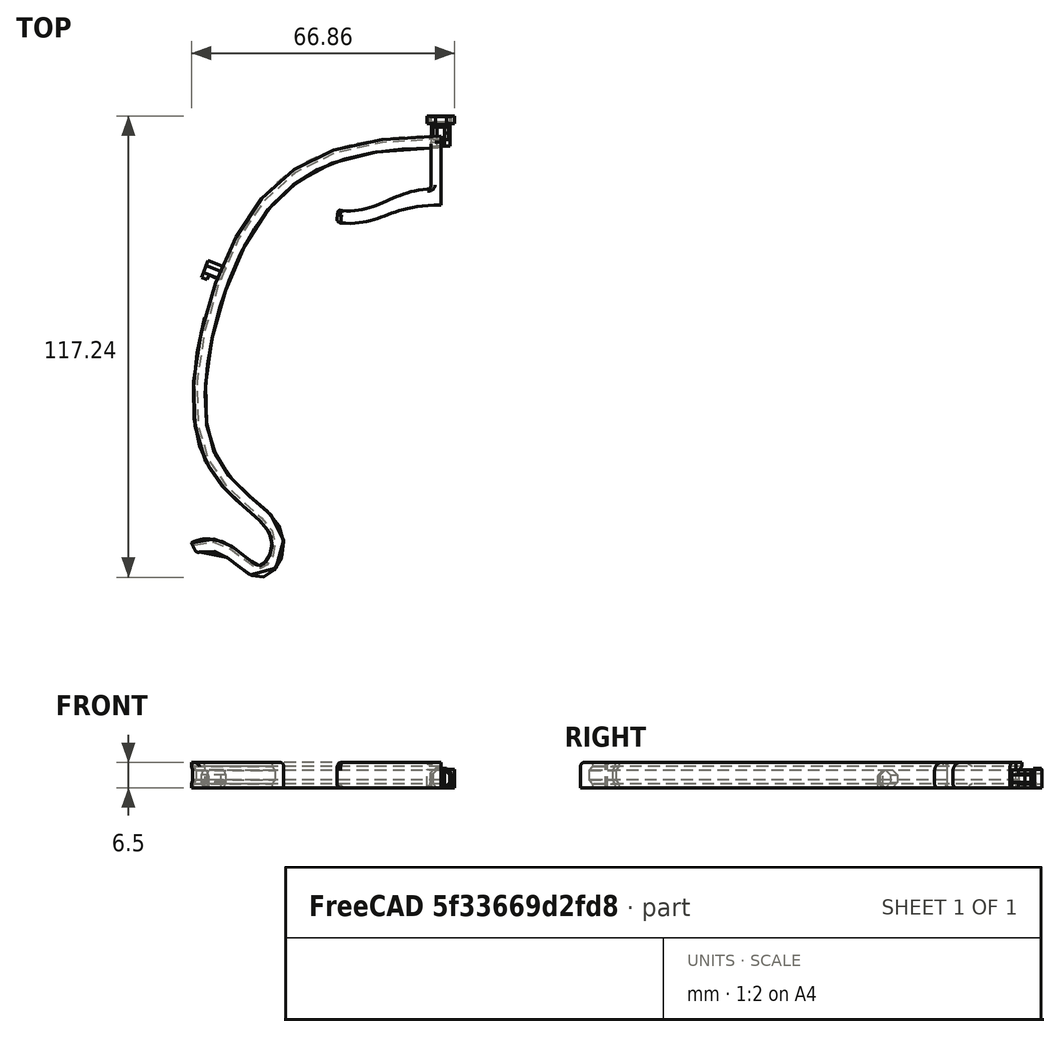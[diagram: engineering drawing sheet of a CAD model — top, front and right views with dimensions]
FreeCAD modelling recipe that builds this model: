
FCSTD DOCUMENT  (FreeCAD 0.18R16146 (Git))
Label: frame-001-02-c
License: All rights reserved
LicenseURL: http://ja.wikipedia.org/wiki/%E8%91%97%E4%BD%9C%E6%A8%A9%E8%A1%A8%E7%A4%BA
objects: Sketcher::SketchObject×5, Part::Extrusion×5, Part::Box×3, Part::Cut×2, Part::Fillet×2, Part::Compound×2, Mesh::Feature×1, Part::Sweep×1, Part::Mirroring×1, Part::MultiCommon×1
note: 22 computed .brp shape members not serialized (recipe doc carries the construction recipe); baked Part::Feature solids carry a one-line shape summary decoded from their .brp

FEATURE [Sketcher::SketchObject] Sketch  label="Sketch_FrameShape"
  sketch-geometry (15):
    g0-g7: Circle [constr] x8 (B-spline internal-alignment scaffolding for g8; pole/knot coordinates omitted)
    g8: BSplineCurve PolesCount=8 KnotsCount=6 Degree=3 IsPeriodic=0
    g9-g14: GeomPoint [constr] x6 (B-spline internal-alignment scaffolding for g8; pole/knot coordinates omitted)
  constraints (6):
    c: Radius(g0) = 6
    c: Equal(g0, g1-g6) x6
    c: InternalAlignment(g0-g7 -> g8) x8
    c: InternalAlignment(g9-g14 -> g8) x6
    c: Horizontal(g1,g8)
    c: Coincident(g-1,g8)
FEATURE [Sketcher::SketchObject] Sketch001
  Placement = pos=(0,0,0) rot=(0.57735,0.57735,0.57735;2.0944rad)
  sketch-geometry (8):
    g0: LineSegment StartX=-0.5 StartY=6.5 StartZ=0 EndX=2.5 EndY=6.5 EndZ=0
    g1: LineSegment StartX=2.5 StartY=6.5 StartZ=0 EndX=2.5 EndY=5.5 EndZ=0
    g2: LineSegment StartX=2.5 StartY=0 StartZ=0 EndX=-0.5 EndY=0 EndZ=0
    g3: LineSegment StartX=-0.5 StartY=0 StartZ=0 EndX=-0.5 EndY=6.5 EndZ=0
    g4: LineSegment StartX=2.5 StartY=5.5 StartZ=0 EndX=1.7 EndY=4.5 EndZ=0
    g5: LineSegment StartX=1.7 StartY=4.5 StartZ=0 EndX=1.7 EndY=2 EndZ=0
    g6: LineSegment StartX=1.7 StartY=2 StartZ=0 EndX=2.5 EndY=1 EndZ=0
    g7: LineSegment StartX=2.5 StartY=1 StartZ=0 EndX=2.5 EndY=0 EndZ=0
  constraints (24):
    c: Coincident(g0,g1)
    c: Coincident(g2,g3)
    c: Coincident(g3,g0)
    c: Horizontal(g0)
    c: Horizontal(g2)
    c: Vertical(g1)
    c: Vertical(g3)
    c: DistanceX(g0,g0) = 3
    c: DistanceY(g1,g0) = 1
    c: DistanceX(g-1,g2) = -0.5
    c: PointOnObject(g2,g-1)
    c: DistanceY(g2,g0) = 6.5
    c: Coincident(g1,g4)
    c: Coincident(g4,g5)
    c: Vertical(g5)
    c: Coincident(g5,g6)
    c: Coincident(g6,g7)
    c: Coincident(g7,g2)
    c: DistanceX(g2,g2) = 3
    c: Vertical(g7)
    c: DistanceY(g2,g6) = 1
    c: DistanceY(g6,g5) = 1
    c: DistanceY(g4,g1) = 1
    c: DistanceX(g2,g5) = 2.2
FEATURE [Mesh::Feature] cd43cbcc_75a4_11ea_893f_42010a00001e_UM3E_Visor_frame_EUROPE_ISO838_v3  label="cd43cbcc-75a4-11ea-893f-42010a00001e_UM3E_Visor_frame_EUROPE_ISO838_v3"
  Placement = pos=(0,-59,0) rot=(0,0,1;0rad)
FEATURE [Sketcher::SketchObject] Sketch002  label="OctPinSketch"
  Placement = pos=(0,0,0) rot=(1,0,0;1.5708rad)
  sketch-geometry (9):
    g0: LineSegment StartX=2.3097 StartY=1.35299 StartZ=0 EndX=2.3097 EndY=3.26641 EndZ=0
    g1: LineSegment StartX=2.3097 StartY=3.26641 StartZ=0 EndX=0.956709 EndY=4.6194 EndZ=0
    g2: LineSegment StartX=0.956709 StartY=4.6194 StartZ=0 EndX=-0.956709 EndY=4.6194 EndZ=0
    g3: LineSegment StartX=-0.956709 StartY=4.6194 StartZ=0 EndX=-2.3097 EndY=3.26641 EndZ=0
    g4: LineSegment StartX=-2.3097 StartY=3.26641 StartZ=0 EndX=-2.3097 EndY=1.35299 EndZ=0
    g5: LineSegment StartX=-2.3097 StartY=1.35299 StartZ=0 EndX=-0.956709 EndY=0 EndZ=0
    g6: LineSegment StartX=-0.956709 StartY=0 StartZ=0 EndX=0.956709 EndY=0 EndZ=0
    g7: LineSegment StartX=0.956709 StartY=0 StartZ=0 EndX=2.3097 EndY=1.35299 EndZ=0
    g8: Circle [constr] CenterX=0 CenterY=2.3097 CenterZ=0 NormalX=0 NormalY=0 NormalZ=1 AngleXU=0 Radius=2.5
  constraints (21):
    c: Coincident(g0,g1)
    c: Coincident(g1,g2)
    c: Coincident(g2,g3)
    c: Coincident(g3,g4)
    c: Coincident(g4,g5)
    c: Coincident(g5,g6)
    c: Coincident(g6,g7)
    c: Coincident(g7,g0)
    c: Equal(g0, g1-g7) x7
    c: PointOnObject(g0,g8)
    c: PointOnObject(g1,g8)
    c: PointOnObject(g2,g8)
    c: PointOnObject(g3,g8)
    c: PointOnObject(g4,g8)
    c: PointOnObject(g5,g8)
    c: PointOnObject(g6,g8)
    c: PointOnObject(g7,g8)
    c: Distance(g0,g8) = 2.5
    c: Horizontal(g6)
    c: PointOnObject(g8,g-2)
    c: PointOnObject(g6,g-1)
FEATURE [Part::Extrusion] Extrude002  label="OctPin"
  Base = -> Sketch002
  Dir = (0,-1,0)
  DirMode = 2
  FaceMakerClass = Part::FaceMakerBullseye
  LengthFwd = -6
  LengthRev = 0
  Solid = true
  Symmetric = false
FEATURE [Part::Extrusion] Extrude003  label="OctPinFront"
  Base = -> Sketch002
  Dir = (0,-1,2e-16)
  DirMode = 2
  FaceMakerClass = Part::FaceMakerBullseye
  LengthFwd = -3.8
  LengthRev = 0
  Placement = pos=(0,3,0) rot=(0,0,1;0rad)
  Solid = true
  Symmetric = false
FEATURE [Part::Extrusion] Extrude004  label="OctPin_WNotch_column"
  Base = -> Sketch002
  Dir = (0,-1,2e-16)
  DirMode = 2
  FaceMakerClass = Part::FaceMakerBullseye
  LengthFwd = -4.8
  LengthRev = 0
  Solid = true
  Symmetric = false
FEATURE [Part::Box] Box008  label="立方体008"
  AttacherType = Attacher::AttachEngine3D
  Height = 6
  Length = 2
  Placement = pos=(1,0,-0.5) rot=(0,0,1;0rad)
  Width = 3.3
FEATURE [Part::Cut] Cut  label="OctPin_WNotch"
  Base = -> Extrude004
  Tool = -> Box008
FEATURE [Part::Cut] Cut001  label="OctPin_WNotchR"
  Base = -> Extrude004
  Placement = pos=(55.5,-33.1,0) rot=(0,0,-1;1.18682rad)
  Tool = -> Box008
FEATURE [Sketcher::SketchObject] Sketch003
  sketch-geometry (18):
    g0: LineSegment StartX=0 StartY=1 StartZ=0 EndX=0 EndY=-15 EndZ=0
    g1: LineSegment StartX=2.5 StartY=-11 StartZ=0 EndX=2.5 EndY=1 EndZ=0
    g2: LineSegment StartX=2.5 StartY=1 StartZ=0 EndX=0 EndY=1 EndZ=0
    g3: LineSegment StartX=26.0693 StartY=-16.3 StartZ=0 EndX=26.4803 EndY=-19.4735 EndZ=0
    g4-g7: Circle [constr] x4 (B-spline internal-alignment scaffolding for g8; pole/knot coordinates omitted)
    g8: BSplineCurve PolesCount=4 KnotsCount=2 Degree=3 IsPeriodic=0
    g9: GeomPoint [constr] X=2.5 Y=-11 Z=0
    g10: GeomPoint [constr] X=26.0693 Y=-16.3 Z=0
    g11-g14: Circle [constr] x4 (B-spline internal-alignment scaffolding for g15; pole/knot coordinates omitted)
    g15: BSplineCurve PolesCount=4 KnotsCount=2 Degree=3 IsPeriodic=0
    g16: GeomPoint [constr] X=0 Y=-15 Z=0
    g17: GeomPoint [constr] X=26.4803 Y=-19.4735 Z=0
  constraints (32):
    c: PointOnObject(g0,g-2)
    c: Vertical(g0)
    c: Vertical(g1)
    c: Coincident(g1,g2)
    c: Coincident(g2,g0)
    c: DistanceX(g0,g1) = 2.5
    c: Horizontal(g2)
    c: DistanceY(g-1,g0) = 1
    c: DistanceY(g3,g1) = 5.3
    c: DistanceY(g0,g1) = 4
    c: DistanceY(g0,g-1) = 15
    c: Coincident(g8,g1)
    c: Radius(g4) = 2
    c: Equal(g4,g5)
    c: Equal(g4,g6)
    c: Equal(g4,g7)
    c: Coincident(g8,g3)
    c: InternalAlignment(g4-g7 -> g8) x4
    c: InternalAlignment(g9,g8)
    c: InternalAlignment(g10,g8)
    c: Coincident(g15,g0)
    c: Radius(g11) = 2
    c: Equal(g11,g12)
    c: Equal(g11,g13)
    c: Equal(g11,g14)
    c: Coincident(g15,g3)
    c: InternalAlignment(g11-g14 -> g15) x4
    c: InternalAlignment(g16,g15)
    c: InternalAlignment(g17,g15)
    c: Distance(g3,g3) = 3.2
    c: Horizontal(g0,g12)
    c: Horizontal(g5,g1)
FEATURE [Part::Extrusion] Extrude
  Base = -> Sketch003
  Dir = (0,0,1)
  DirMode = 2
  FaceMakerClass = Part::FaceMakerBullseye
  LengthFwd = 6.5
  LengthRev = 0
  Solid = true
  Symmetric = false
FEATURE [Part::Fillet] Fillet  label="AGOATE_R"
  Base = -> Extrude
  Edges = 11 edges: [Edge1 r=1,Edge3 r=1,Edge4 r=1,Edge11 r=1,Edge12 r=1,Edge13 r=2,Edge14 r=0.5,Edge15 r=1,Edge16 r=1,Edge17 r=0.5,Edge18 r=0.5]
FEATURE [Part::Sweep] Sweep  label="Sweep_RightFrame"
  Frenet = false
  Sections = -> [Sketch001]
  Solid = true
  Spine = -> Sketch [Edge1]
  Transition = 1
FEATURE [Part::Fillet] Fillet001  label="Fillet_Sweep_RightFrame"
  Base = -> Sweep
  Edges = 2 edges r=1: [Edge1,Edge24]
FEATURE [Part::Compound] Compound  label="RightSide"
  Links = -> [Cut001,Fillet,Fillet001]
FEATURE [Part::Mirroring] Part__Mirroring001  label="LeftSide (Mirrored)"
  Base = (0,0,0)
  Normal = (1,0,0)
  Source = -> Compound
FEATURE [Part::Box] Box  label="立方体"
  AttacherType = Attacher::AttachEngine3D
  Height = 10
  Length = 4
  Placement = pos=(-2,2.8,0) rot=(0,0,1;0rad)
  Width = 4
FEATURE [Part::Box] Box010  label="立方体010"
  AttacherType = Attacher::AttachEngine3D
  Height = 4.7
  Length = 7
  Placement = pos=(-3.5,5.6,0) rot=(0,0,1;0rad)
  Width = 2
FEATURE [Part::MultiCommon] Common  label="前ダボ柱"
  Shapes = -> [Extrude003,Box]
FEATURE [Sketcher::SketchObject] Sketch004
  MapMode = 5
  Placement = pos=(0,6.8,0) rot=(0,0.707107,0.707107;3.14159rad)
  Support = -> [Common]
  sketch-geometry (8):
    g0: LineSegment StartX=-2.34451 StartY=0 StartZ=0 EndX=-2.75 EndY=1.00428 EndZ=0
    g1: LineSegment StartX=-2.75 StartY=1.00428 StartZ=0 EndX=-2.75 EndY=3.6504 EndZ=0
    g2: LineSegment StartX=-2.75 StartY=3.6504 StartZ=0 EndX=-1.4004 EndY=5 EndZ=0
    g3: LineSegment StartX=-1.4004 StartY=5 StartZ=0 EndX=1.4004 EndY=5 EndZ=0
    g4: LineSegment StartX=1.4004 StartY=5 StartZ=0 EndX=2.75 EndY=3.6504 EndZ=0
    g5: LineSegment StartX=2.75 StartY=3.6504 StartZ=0 EndX=2.75 EndY=1.00428 EndZ=0
    g6: LineSegment StartX=2.75 StartY=1.00428 StartZ=0 EndX=2.34451 EndY=0 EndZ=0
    g7: LineSegment StartX=2.34451 StartY=0 StartZ=0 EndX=-2.34451 EndY=0 EndZ=0
  constraints (17):
    c: Coincident(g0,g1)
    c: Coincident(g1,g2)
    c: Coincident(g2,g3)
    c: Coincident(g3,g4)
    c: Coincident(g4,g5)
    c: Coincident(g5,g6)
    c: Coincident(g6,g7)
    c: Coincident(g7,g0)
    c: Vertical(g1)
    c: Symmetric(g0,g6,g-2)
    c: Symmetric(g0,g5,g-2)
    c: Symmetric(g1,g4,g-2)
    c: Symmetric(g2,g3,g-2)
    c: PointOnObject(g6,g-1)
    c: DistanceY(g6,g3) = 5
    c: DistanceX(g0,g5) = 5.5
    c: Angle(g5,g4,g4) = 0.785398
FEATURE [Part::Extrusion] Extrude005  label="前ダボトメ"
  Base = -> Sketch004
  Dir = (0,1,-2e-16)
  DirMode = 2
  FaceMakerClass = Part::FaceMakerBullseye
  LengthFwd = 2
  LengthRev = 0
  Solid = true
  Symmetric = false
FEATURE [Part::Compound] Compound001  label="前ダボ"
  Links = -> [Common,Extrude005]
  Placement = pos=(0,-1.4,0) rot=(0,0,1;0rad)
